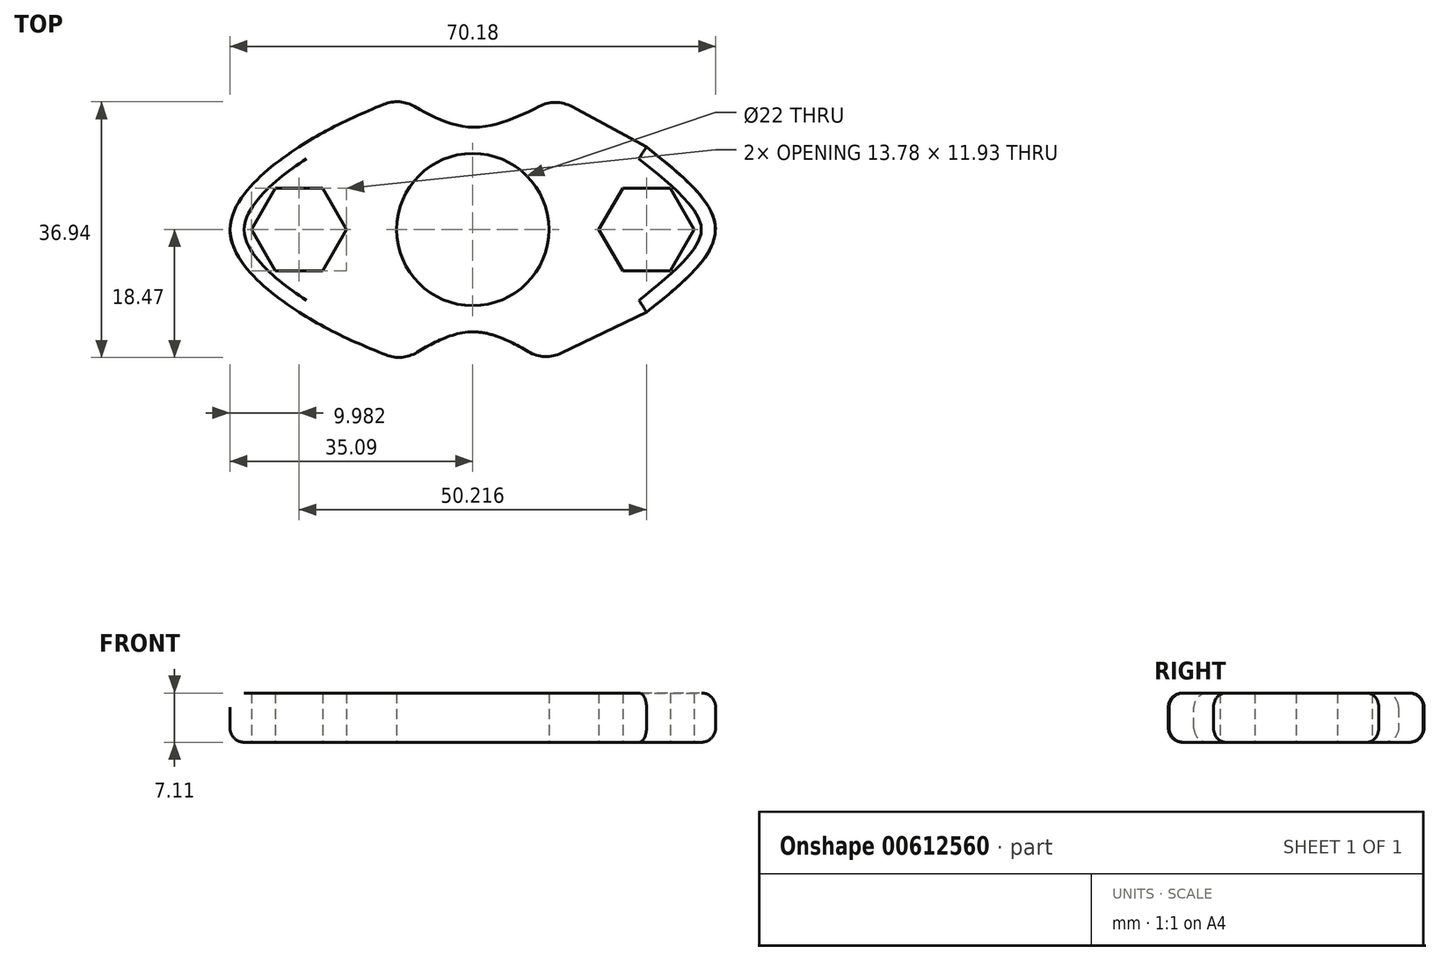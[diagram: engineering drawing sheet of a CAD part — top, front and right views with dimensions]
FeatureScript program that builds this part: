
annotation { "Feature Type Name" : "Feature", "Feature Type Description" : "" }
export const myFeature = defineFeature(function(context is Context, id is Id, definition is map)
    precondition{}
    {
        {
            var Q0;
            Q0=qCreatedBy(makeId("Top.planeOp"),FACE);
            var sketch = newSketch(context, id + "F0", { "sketchPlane" : qUnion([Q0])});
            skLineSegment(sketch, "E0.right", {"start": v(-35.09, -0.02) * mm, "end": v(-35.09, 0) * mm});
            skPoint(sketch, "E0.middle", {"position": v(0, 0) * mm});
            skCircle(sketch, "E1", {"center": v(0, 0) * mm, "radius": 11 * mm});
            skLineSegment(sketch, "E2", {"start": v(0, -19.05) * mm, "end": v(0, -14.78) * mm});
            skFitSpline(sketch, "E3", {"points": [v(11.93, 19.05) * mm, v(0, 14.78) * mm, v(-10.5, 19.05) * mm], "startDerivative": vector(-23.63, -12.7) * mm, "endDerivative": vector(-21.22, 12.94) * mm});
            skFitSpline(sketch, "E4", {"points": [v(10.34, -19.05) * mm, v(0, -14.78) * mm, v(-10.15, -19.05) * mm], "startDerivative": vector(-20.65, 12.8) * mm, "endDerivative": vector(-20.33, -12.83) * mm});
            skLineSegment(sketch, "E5", {"start": v(0, 0) * mm, "end": v(25.1, 0) * mm});
            skLineSegment(sketch, "E6", {"start": v(25.1, 0) * mm, "end": v(0, 0) * mm});
            skLineSegment(sketch, "E7", {"start": v(0, 0) * mm, "end": v(-25.1, 0) * mm});
            skLineSegment(sketch, "E8", {"start": v(-25.1, 0) * mm, "end": v(-25.1, 11.93) * mm});
            skLineSegment(sketch, "E9", {"start": v(-25.1, 11.93) * mm, "end": v(-25.1, 0) * mm});
            skLineSegment(sketch, "E10", {"start": v(-25.1, 0) * mm, "end": v(-25.1, -11.93) * mm});
            skLineSegment(sketch, "E11", {"start": v(25.1, 0) * mm, "end": v(25.1, 11.93) * mm});
            skLineSegment(sketch, "E12", {"start": v(25.1, 11.93) * mm, "end": v(25.1, 0) * mm});
            skFitSpline(sketch, "E13", {"points": [v(11.93, 19.05) * mm, v(25.1, 11.93) * mm], "startDerivative": vector(13.18, -7.12) * mm, "endDerivative": vector(13.18, -7.12) * mm});
            skLineSegment(sketch, "E14", {"start": v(25.1, 0) * mm, "end": v(25.1, -11.93) * mm});
            skFitSpline(sketch, "E15", {"points": [v(10.34, -19.05) * mm, v(25.1, -11.93) * mm], "startDerivative": vector(14.77, 7.12) * mm, "endDerivative": vector(14.77, 7.12) * mm});
            skFitSpline(sketch, "E16", {"points": [v(-10.5, 19.05) * mm, v(-25.1, 11.93) * mm, v(-35.09, 0) * mm, v(-25.1, -11.93) * mm, v(-10.15, -19.05) * mm], "startDerivative": vector(-57.14, -23.16) * mm, "endDerivative": vector(58.19, -22.78) * mm});
            skPoint(sketch, "E17.start.orphan", {"position": v(0, 19.05) * mm});
            skPoint(sketch, "E18.end.orphan", {"position": v(35.09, 0) * mm});
            skFitSpline(sketch, "E19", {"points": [v(25.1, 11.93) * mm, v(35.09, 0) * mm, v(25.1, -11.93) * mm], "startDerivative": vector(29.93, -23.86) * mm, "endDerivative": vector(-29.93, -23.86) * mm});
            skPoint(sketch, "E20.orphan", {"position": v(35.09, -19.05) * mm});
            skPoint(sketch, "E0.top.start.orphan", {"position": v(35.09, 19.05) * mm});
            skPoint(sketch, "E21.orphan", {"position": v(-35.09, 19.05) * mm});
            skPoint(sketch, "E22.trimOffspring.end.orphan", {"position": v(-35.09, -19.05) * mm});
            skCircle(sketch, "E23.cCircle", {"center": v(25.1, 0) * mm, "radius": 5.97 * mm, "construction": true});
            skLineSegment(sketch, "E23.0", {"start": v(28.55, -5.97) * mm, "end": v(21.66, -5.97) * mm});
            skLineSegment(sketch, "E23.1", {"start": v(21.66, -5.97) * mm, "end": v(18.22, 0) * mm});
            skLineSegment(sketch, "E23.2", {"start": v(18.22, 0) * mm, "end": v(21.66, 5.97) * mm});
            skLineSegment(sketch, "E23.3", {"start": v(21.66, 5.97) * mm, "end": v(28.55, 5.97) * mm});
            skLineSegment(sketch, "E23.4", {"start": v(28.55, 5.97) * mm, "end": v(32, 0) * mm});
            skLineSegment(sketch, "E23.5", {"start": v(32, 0) * mm, "end": v(28.55, -5.97) * mm});
            skPoint(sketch, "E23.0.midPoint", {"position": v(25.1, -5.97) * mm});
            skCircle(sketch, "E24.cCircle", {"center": v(-25.1, 0) * mm, "radius": 5.97 * mm, "construction": true});
            skLineSegment(sketch, "E24.0", {"start": v(-21.66, -5.97) * mm, "end": v(-28.55, -5.97) * mm});
            skLineSegment(sketch, "E24.1", {"start": v(-28.55, -5.97) * mm, "end": v(-32, 0) * mm});
            skLineSegment(sketch, "E24.2", {"start": v(-32, 0) * mm, "end": v(-28.55, 5.97) * mm});
            skLineSegment(sketch, "E24.3", {"start": v(-28.55, 5.97) * mm, "end": v(-21.66, 5.97) * mm});
            skLineSegment(sketch, "E24.4", {"start": v(-21.66, 5.97) * mm, "end": v(-18.22, 0) * mm});
            skLineSegment(sketch, "E24.5", {"start": v(-18.22, 0) * mm, "end": v(-21.66, -5.97) * mm});
            skPoint(sketch, "E24.0.midPoint", {"position": v(-25.1, -5.97) * mm});
            skSolve(sketch);
        }
        {
            var Q0;
            Q0 = qSketchRegion(id + "F0", true);
            extrude(context, id + "F1", {"entities" : qUnion([Q0]), "depth" : 7.11 * mm, "offsetDistance" : 25.4 * mm});
        }
        {
            var Q0;
            Q0=makeQuery(id+"F1.opExtrude","CAP_EDGE",EDGE,{"disambiguationData":[OSD([sQuery(id+"F0.wireOp",EDGE,"E16")])],"isStart":false});
            var Q1;
            Q1=makeQuery(id+"F1.opExtrude","CAP_EDGE",EDGE,{"disambiguationData":[OSD([sQuery(id+"F0.wireOp",EDGE,"E16")])],"isStart":true});
            var Q2;
            Q2=makeQuery(id+"F1.opExtrude","CAP_EDGE",EDGE,{"disambiguationData":[OSD([sQuery(id+"F0.wireOp",EDGE,"E19")])],"isStart":true});
            var Q3;
            Q3=makeQuery(id+"F1.opExtrude","CAP_EDGE",EDGE,{"disambiguationData":[OSD([sQuery(id+"F0.wireOp",EDGE,"E13")])],"isStart":true});
            var Q4;
            Q4=makeQuery(id+"F1.opExtrude","CAP_EDGE",EDGE,{"disambiguationData":[OSD([sQuery(id+"F0.wireOp",EDGE,"E15")])],"isStart":true});
            var Q5;
            Q5=makeQuery(id+"F1.opExtrude","CAP_EDGE",EDGE,{"disambiguationData":[OSD([sQuery(id+"F0.wireOp",EDGE,"E4")])],"isStart":true});
            var Q6;
            Q6=makeQuery(id+"F1.opExtrude","CAP_EDGE",EDGE,{"disambiguationData":[OSD([sQuery(id+"F0.wireOp",EDGE,"E3")])],"isStart":true});
            var Q7;
            Q7=makeQuery(id+"F1.opExtrude","CAP_EDGE",EDGE,{"disambiguationData":[OSD([sQuery(id+"F0.wireOp",EDGE,"E13")])],"isStart":false});
            var Q8;
            Q8=makeQuery(id+"F1.opExtrude","CAP_EDGE",EDGE,{"disambiguationData":[OSD([sQuery(id+"F0.wireOp",EDGE,"E19")])],"isStart":false});
            var Q9;
            Q9=makeQuery(id+"F1.opExtrude","CAP_EDGE",EDGE,{"disambiguationData":[OSD([sQuery(id+"F0.wireOp",EDGE,"E15")])],"isStart":false});
            var Q10;
            Q10=makeQuery(id+"F1.opExtrude","CAP_EDGE",EDGE,{"disambiguationData":[OSD([sQuery(id+"F0.wireOp",EDGE,"E4")])],"isStart":false});
            var Q11;
            Q11=makeQuery(id+"F1.opExtrude","CAP_EDGE",EDGE,{"disambiguationData":[OSD([sQuery(id+"F0.wireOp",EDGE,"E3")])],"isStart":false});
            fillet(context, id + "F2", {"entities" : qUnion([Q0, Q1, Q2, Q3, Q4, Q5, Q6, Q7, Q8, Q9, Q10, Q11]), "radius" : 2.03 * mm, "tangentPropagation" : true, "allowEdgeOverflow" : false});
        }
        {
            var Q0;
            Q0=makeQuery(id+"F1.opExtrude","SWEPT_EDGE",EDGE,{"disambiguationData":[OSD([sQuery(id+"F0.wireOp",EDGE,"E3"),sQuery(id+"F0.wireOp",EDGE,"E13")])]});
            var Q1;
            Q1=makeQuery(id+"F1.opExtrude","SWEPT_EDGE",EDGE,{"disambiguationData":[OSD([sQuery(id+"F0.wireOp",EDGE,"E3"),sQuery(id+"F0.wireOp",EDGE,"E16")])]});
            var Q2;
            Q2=makeQuery(id+"F1.opExtrude","SWEPT_EDGE",EDGE,{"disambiguationData":[OSD([sQuery(id+"F0.wireOp",EDGE,"E4"),sQuery(id+"F0.wireOp",EDGE,"E15")])]});
            var Q3;
            Q3=makeQuery(id+"F1.opExtrude","SWEPT_EDGE",EDGE,{"disambiguationData":[OSD([sQuery(id+"F0.wireOp",EDGE,"E4"),sQuery(id+"F0.wireOp",EDGE,"E16")])]});
            fillet(context, id + "F3", {"entities" : qUnion([Q0, Q1, Q2, Q3]), "radius" : 5.08 * mm, "tangentPropagation" : true, "allowEdgeOverflow" : false});
        }
    });
